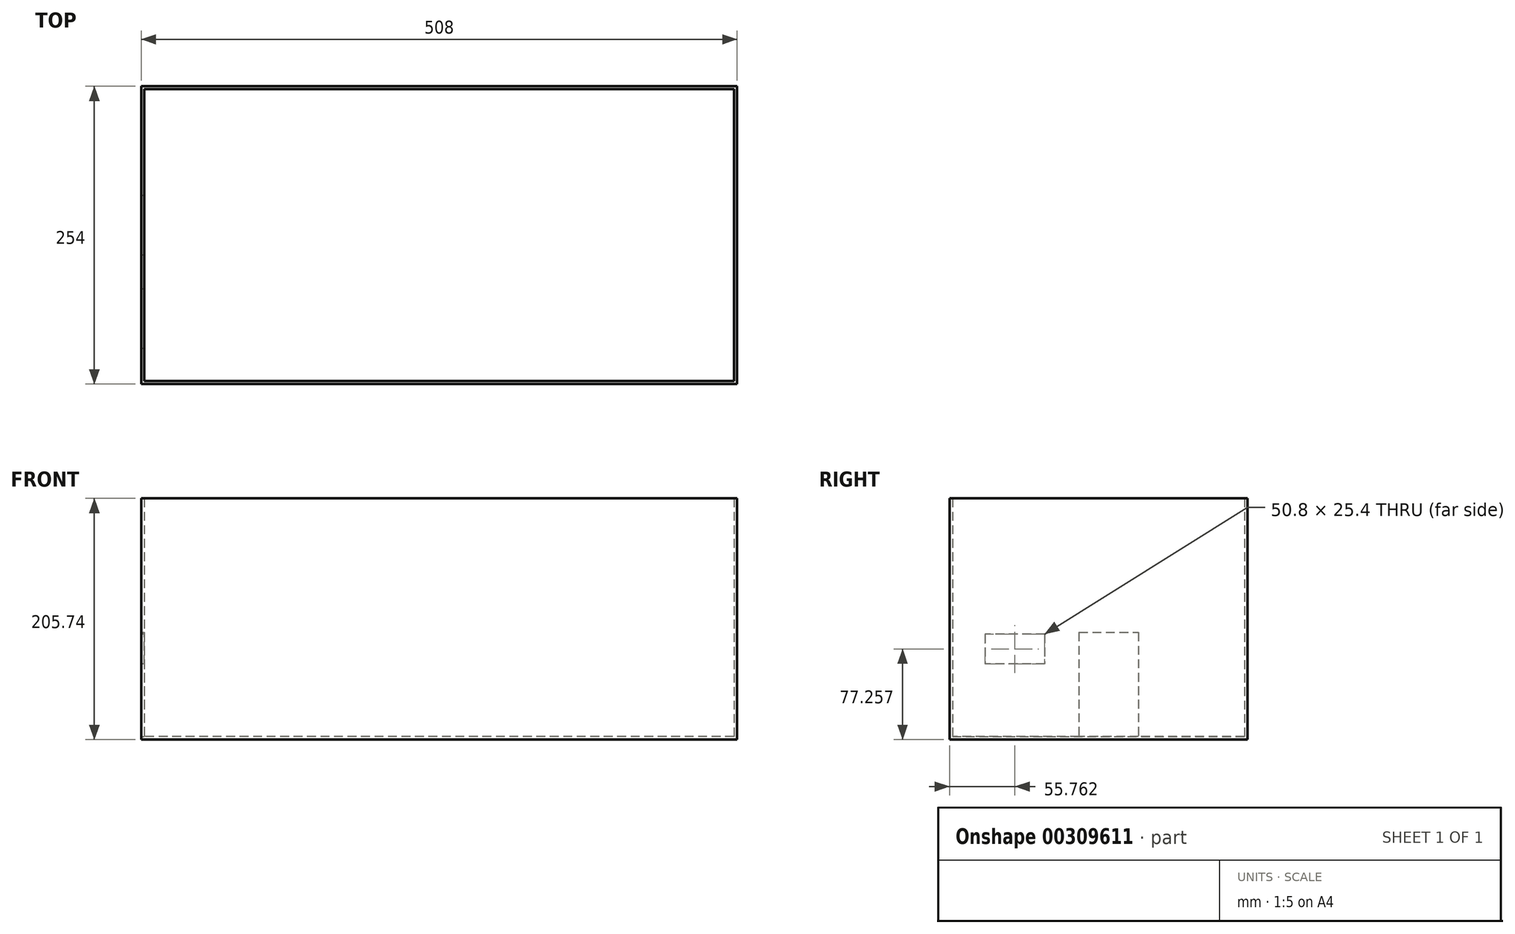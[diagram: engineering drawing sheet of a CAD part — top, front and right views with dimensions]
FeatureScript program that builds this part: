
annotation { "Feature Type Name" : "Feature", "Feature Type Description" : "" }
export const myFeature = defineFeature(function(context is Context, id is Id, definition is map)
    precondition{}
    {
        {
            var Q0;
            Q0=qCreatedBy(makeId("Top.planeOp"),FACE);
            var sketch = newSketch(context, id + "F0", { "sketchPlane" : qUnion([Q0])});
            skLineSegment(sketch, "E0.bottom", {"start": v(254, 127) * mm, "end": v(-254, 127) * mm});
            skLineSegment(sketch, "E0.top", {"start": v(254, -127) * mm, "end": v(-254, -127) * mm});
            skLineSegment(sketch, "E0.left", {"start": v(254, 127) * mm, "end": v(254, -127) * mm});
            skLineSegment(sketch, "E0.right", {"start": v(-254, 127) * mm, "end": v(-254, -127) * mm});
            skPoint(sketch, "E0.middle", {"position": v(0, 0) * mm});
            skSolve(sketch);
        }
        {
            var Q0;
            Q0 = qSketchRegion(id + "F0", true);
            extrude(context, id + "F1", {"entities" : qUnion([Q0]), "depth" : 2.54 * mm});
        }
        {
            var Q0;
            Q0=makeQuery(id+"F1.opExtrude","CAP_FACE",FACE,{"disambiguationData":[OSD([sQuery(id+"F0.wireOp",EDGE,"E0.bottom"),sQuery(id+"F0.wireOp",EDGE,"E0.top"),sQuery(id+"F0.wireOp",EDGE,"E0.left"),sQuery(id+"F0.wireOp",EDGE,"E0.right")])],"isStart":false});
            var sketch = newSketch(context, id + "F2", { "sketchPlane" : qUnion([Q0])});
            skLineSegment(sketch, "E1.bottom", {"start": v(-254, 127) * mm, "end": v(-251.46, 127) * mm});
            skLineSegment(sketch, "E1.top", {"start": v(-254, -127) * mm, "end": v(-251.46, -127) * mm});
            skLineSegment(sketch, "E1.left", {"start": v(-254, 127) * mm, "end": v(-254, -127) * mm});
            skLineSegment(sketch, "E1.right", {"start": v(-251.46, 127) * mm, "end": v(-251.46, -127) * mm});
            skSolve(sketch);
        }
        {
            var Q0;
            Q0=makeQuery(id+"F2.imprint","IMPRINT",FACE,{"disambiguationData":[TD([[makeQuery(id+"F2.imprint","IMPRINT",EDGE,{"derivedFrom":sQuery(id+"F2.wireOp",EDGE,"E1.bottom")}),1.0]])]});
            extrude(context, id + "F3", {"entities" : qUnion([Q0]), "operationType" : NewBodyOperationType.ADD, "depth" : 203.2 * mm});
        }
        {
            var Q0;
            Q0=makeQuery(id+"F1.opExtrude","CAP_FACE",FACE,{"disambiguationData":[OSD([sQuery(id+"F0.wireOp",EDGE,"E0.bottom"),sQuery(id+"F0.wireOp",EDGE,"E0.top"),sQuery(id+"F0.wireOp",EDGE,"E0.left"),sQuery(id+"F0.wireOp",EDGE,"E0.right")])],"isStart":false});
            var sketch = newSketch(context, id + "F4", { "sketchPlane" : qUnion([Q0])});
            skLineSegment(sketch, "E2.bottom", {"start": v(254, 127) * mm, "end": v(-251.46, 127) * mm});
            skLineSegment(sketch, "E2.top", {"start": v(254, 124.46) * mm, "end": v(-251.46, 124.46) * mm});
            skLineSegment(sketch, "E2.left", {"start": v(254, 127) * mm, "end": v(254, 124.46) * mm});
            skLineSegment(sketch, "E2.right", {"start": v(-251.46, 127) * mm, "end": v(-251.46, 124.46) * mm});
            skSolve(sketch);
        }
        {
            var Q0;
            Q0=makeQuery(id+"F4.imprint","IMPRINT",FACE,{"disambiguationData":[TD([[makeQuery(id+"F4.imprint","IMPRINT",EDGE,{"derivedFrom":sQuery(id+"F4.wireOp",EDGE,"E2.bottom")}),1.0]])]});
            extrude(context, id + "F5", {"entities" : qUnion([Q0]), "operationType" : NewBodyOperationType.ADD, "depth" : 203.2 * mm});
        }
        {
            var Q0;
            Q0=makeQuery(id+"F1.opExtrude","CAP_FACE",FACE,{"disambiguationData":[OSD([sQuery(id+"F0.wireOp",EDGE,"E0.bottom"),sQuery(id+"F0.wireOp",EDGE,"E0.top"),sQuery(id+"F0.wireOp",EDGE,"E0.left"),sQuery(id+"F0.wireOp",EDGE,"E0.right")])],"isStart":false});
            var sketch = newSketch(context, id + "F6", { "sketchPlane" : qUnion([Q0])});
            skLineSegment(sketch, "E3.bottom", {"start": v(254, -127) * mm, "end": v(251.46, -127) * mm});
            skLineSegment(sketch, "E3.top", {"start": v(254, 124.46) * mm, "end": v(251.46, 124.46) * mm});
            skLineSegment(sketch, "E3.left", {"start": v(254, -127) * mm, "end": v(254, 124.46) * mm});
            skLineSegment(sketch, "E3.right", {"start": v(251.46, -127) * mm, "end": v(251.46, 124.46) * mm});
            skSolve(sketch);
        }
        {
            var Q0;
            Q0=makeQuery(id+"F6.imprint","IMPRINT",FACE,{"disambiguationData":[TD([[makeQuery(id+"F6.imprint","IMPRINT",EDGE,{"derivedFrom":sQuery(id+"F6.wireOp",EDGE,"E3.bottom")}),-1.0]])]});
            extrude(context, id + "F7", {"entities" : qUnion([Q0]), "operationType" : NewBodyOperationType.ADD, "depth" : 203.2 * mm});
        }
        {
            var Q0;
            Q0=makeQuery(id+"F1.opExtrude","CAP_FACE",FACE,{"disambiguationData":[OSD([sQuery(id+"F0.wireOp",EDGE,"E0.bottom"),sQuery(id+"F0.wireOp",EDGE,"E0.top"),sQuery(id+"F0.wireOp",EDGE,"E0.left"),sQuery(id+"F0.wireOp",EDGE,"E0.right")])],"isStart":false});
            var sketch = newSketch(context, id + "F8", { "sketchPlane" : qUnion([Q0])});
            skLineSegment(sketch, "E4.bottom", {"start": v(251.46, -127) * mm, "end": v(-251.46, -127) * mm});
            skLineSegment(sketch, "E4.top", {"start": v(251.46, -124.46) * mm, "end": v(-251.46, -124.46) * mm});
            skLineSegment(sketch, "E4.left", {"start": v(251.46, -127) * mm, "end": v(251.46, -124.46) * mm});
            skLineSegment(sketch, "E4.right", {"start": v(-251.46, -127) * mm, "end": v(-251.46, -124.46) * mm});
            skSolve(sketch);
        }
        {
            var Q0;
            Q0=makeQuery(id+"F8.imprint","IMPRINT",FACE,{"disambiguationData":[TD([[makeQuery(id+"F8.imprint","IMPRINT",EDGE,{"derivedFrom":sQuery(id+"F8.wireOp",EDGE,"E4.bottom")}),-1.0]])]});
            extrude(context, id + "F9", {"entities" : qUnion([Q0]), "operationType" : NewBodyOperationType.ADD, "depth" : 203.2 * mm});
        }
        {
            var Q0;
            Q0=makeQuery(id+"F3.opExtrude","SWEPT_FACE",FACE,{"disambiguationData":[OSD([sQuery(id+"F2.wireOp",EDGE,"E1.right")])]});
            var sketch = newSketch(context, id + "F10", { "sketchPlane" : qUnion([Q0])});
            skLineSegment(sketch, "E5.bottom", {"start": v(-16.59, 91.44) * mm, "end": v(34.21, 91.44) * mm});
            skLineSegment(sketch, "E5.top", {"start": v(-16.59, 2.54) * mm, "end": v(34.21, 2.54) * mm});
            skLineSegment(sketch, "E5.left", {"start": v(-16.59, 91.44) * mm, "end": v(-16.59, 2.54) * mm});
            skLineSegment(sketch, "E5.right", {"start": v(34.21, 91.44) * mm, "end": v(34.21, 2.54) * mm});
            skSolve(sketch);
        }
        {
            var Q0;
            Q0 = qSketchRegion(id + "F10", true);
            extrude(context, id + "F11", {"entities" : qUnion([Q0]), "operationType" : NewBodyOperationType.REMOVE, "oppositeDirection" : true, "depth" : 25.4 * mm});
        }
        {
            var Q0;
            Q0=makeQuery(id+"F3.boolean.opBoolean","MERGE",FACE,{"derivedFrom":[makeQuery(id+"F1.opExtrude","SWEPT_FACE",FACE,{"disambiguationData":[OSD([sQuery(id+"F0.wireOp",EDGE,"E0.right")])]}),makeQuery(id+"F3.opExtrude","SWEPT_FACE",FACE,{"disambiguationData":[OSD([sQuery(id+"F2.wireOp",EDGE,"E1.left")])]})]});
            var sketch = newSketch(context, id + "F12", { "sketchPlane" : qUnion([Q0])});
            skLineSegment(sketch, "E6.bottom", {"start": v(45.84, 89.96) * mm, "end": v(96.64, 89.96) * mm});
            skLineSegment(sketch, "E6.top", {"start": v(45.84, 64.56) * mm, "end": v(96.64, 64.56) * mm});
            skLineSegment(sketch, "E6.left", {"start": v(45.84, 89.96) * mm, "end": v(45.84, 64.56) * mm});
            skLineSegment(sketch, "E6.right", {"start": v(96.64, 89.96) * mm, "end": v(96.64, 64.56) * mm});
            skSolve(sketch);
        }
        {
            var Q0;
            Q0=makeQuery(id+"F12.imprint","IMPRINT",FACE,{"disambiguationData":[TD([[makeQuery(id+"F12.imprint","IMPRINT",EDGE,{"derivedFrom":sQuery(id+"F12.wireOp",EDGE,"E6.bottom")}),-1.0]])]});
            extrude(context, id + "F13", {"entities" : qUnion([Q0]), "operationType" : NewBodyOperationType.REMOVE, "oppositeDirection" : true, "depth" : 25.4 * mm});
        }
    });
